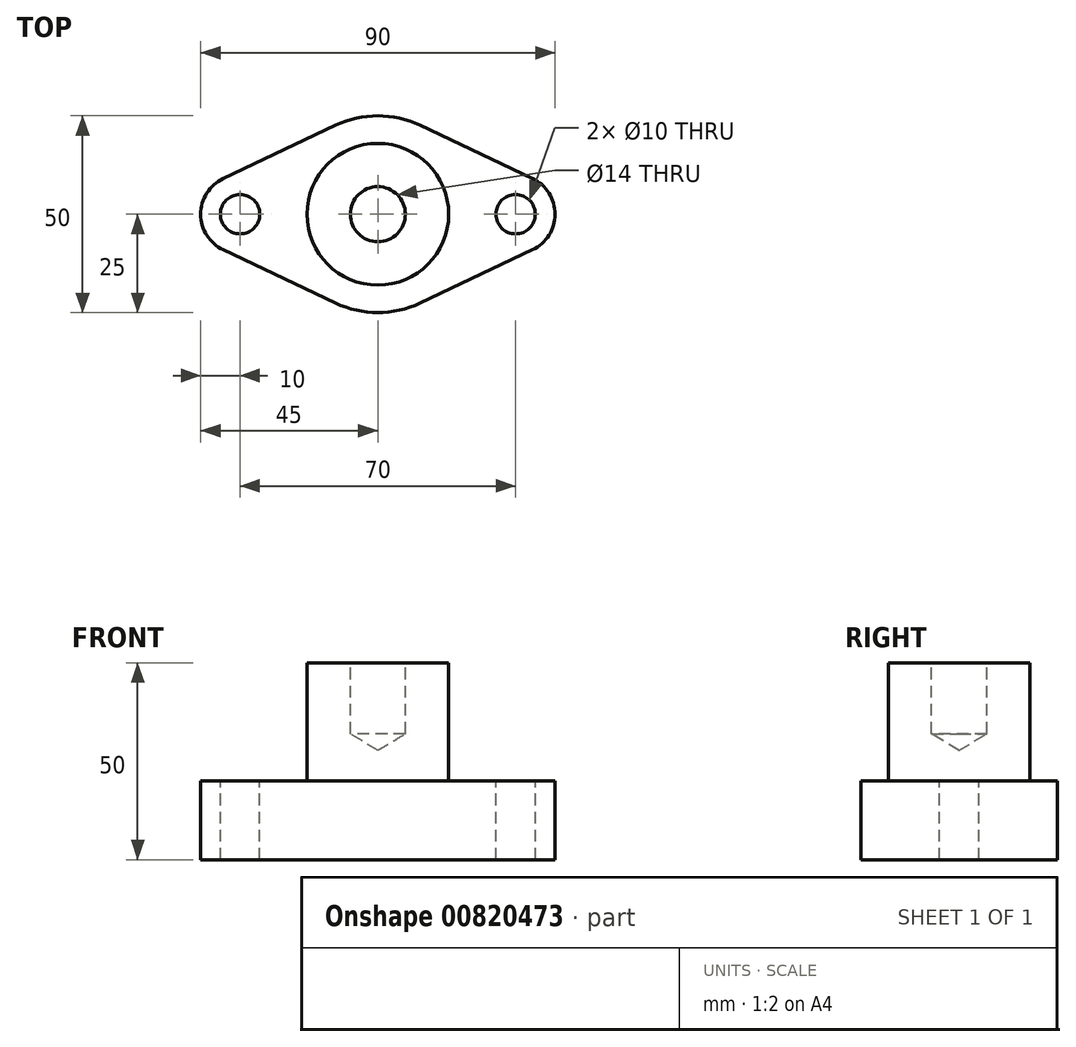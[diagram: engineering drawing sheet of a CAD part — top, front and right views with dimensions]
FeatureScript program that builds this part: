
annotation { "Feature Type Name" : "Feature", "Feature Type Description" : "" }
export const myFeature = defineFeature(function(context is Context, id is Id, definition is map)
    precondition{}
    {
        {
            var Q0;
            Q0=qCreatedBy(makeId("Top.planeOp"),FACE);
            var sketch = newSketch(context, id + "F0", { "sketchPlane" : qUnion([Q0])});
            skCircle(sketch, "E0", {"center": v(0, 0) * mm, "radius": 25 * mm});
            skPoint(sketch, "E1", {"position": v(-35, 0) * mm});
            skCircle(sketch, "E2", {"center": v(-35, 0) * mm, "radius": 10 * mm});
            skPoint(sketch, "E3", {"position": v(35, 0) * mm});
            skCircle(sketch, "E4", {"center": v(35, 0) * mm, "radius": 10 * mm});
            skLineSegment(sketch, "E5", {"start": v(-39.29, 9.04) * mm, "end": v(-10.71, 22.59) * mm});
            skLineSegment(sketch, "E6", {"start": v(10.71, 22.59) * mm, "end": v(39.29, 9.04) * mm});
            skLineSegment(sketch, "E7", {"start": v(-39.29, -9.04) * mm, "end": v(-10.71, -22.59) * mm});
            skLineSegment(sketch, "E8", {"start": v(10.71, -22.59) * mm, "end": v(39.29, -9.04) * mm});
            skSolve(sketch);
        }
        {
            var Q0;
            {var subQ0=sQuery(id+"F0.wireOp",EDGE,"E6");Q0=makeQuery(id+"F0.imprint","IMPRINT",FACE,{"disambiguationData":[TD([[makeQuery(id+"F0.imprint","IMPRINT",EDGE,{"derivedFrom":subQ0}),-1.0]])]});}
            var Q1;
            {var subQ0=sQuery(id+"F0.wireOp",EDGE,"E8");Q1=makeQuery(id+"F0.imprint","IMPRINT",FACE,{"disambiguationData":[TD([[makeQuery(id+"F0.imprint","IMPRINT",EDGE,{"derivedFrom":subQ0}),1.0]])]});}
            var Q2;
            {var subQ0=sQuery(id+"F0.wireOp",EDGE,"E5");Q2=makeQuery(id+"F0.imprint","IMPRINT",FACE,{"disambiguationData":[TD([[makeQuery(id+"F0.imprint","IMPRINT",EDGE,{"derivedFrom":subQ0}),-1.0]])]});}
            var Q3;
            {var subQ0=sQuery(id+"F0.wireOp",EDGE,"E2");var subQ1=makeQuery(id+"F0.imprint","INTERSECT",VERTEX,{"derivedFrom":[subQ0,sQuery(id+"F0.wireOp",EDGE,"E5")]});Q3=makeQuery(id+"F0.imprint","IMPRINT",FACE,{"disambiguationData":[TD([[makeQuery(id+"F0.imprint","IMPRINT",EDGE,{"disambiguationData":[TD([[subQ1,1.0]])],"derivedFrom":subQ0}),1.0]])]});}
            var Q4;
            {var subQ0=sQuery(id+"F0.wireOp",EDGE,"E4");var subQ1=makeQuery(id+"F0.imprint","INTERSECT",VERTEX,{"derivedFrom":[subQ0,sQuery(id+"F0.wireOp",EDGE,"E6")]});Q4=makeQuery(id+"F0.imprint","IMPRINT",FACE,{"disambiguationData":[TD([[makeQuery(id+"F0.imprint","IMPRINT",EDGE,{"disambiguationData":[TD([[subQ1,-1.0]])],"derivedFrom":subQ0}),1.0]])]});}
            var Q5;
            {var subQ0=sQuery(id+"F0.wireOp",EDGE,"E7");Q5=makeQuery(id+"F0.imprint","IMPRINT",FACE,{"disambiguationData":[TD([[makeQuery(id+"F0.imprint","IMPRINT",EDGE,{"derivedFrom":subQ0}),1.0]])]});}
            var Q6;
            {var subQ0=sQuery(id+"F0.wireOp",EDGE,"E0");var subQ4=makeQuery(id+"F0.imprint","INTERSECT",VERTEX,{"derivedFrom":[subQ0,sQuery(id+"F0.wireOp",EDGE,"E6")]});Q6=makeQuery(id+"F0.imprint","IMPRINT",FACE,{"disambiguationData":[TD([[makeQuery(id+"F0.imprint","IMPRINT",EDGE,{"disambiguationData":[TD([[subQ4,1.0]])],"derivedFrom":subQ0}),1.0]])]});}
            extrude(context, id + "F1", {"entities" : qUnion([Q0, Q1, Q2, Q3, Q4, Q5, Q6]), "endBound" : BoundingType.SYMMETRIC, "depth" : 20 * mm, "offsetDistance" : 25 * mm});
        }
        {
            var Q0;
            Q0=makeQuery(id+"F1.opExtrude","CAP_FACE",FACE,{"disambiguationData":[OSD([sQuery(id+"F0.wireOp",EDGE,"E0"),sQuery(id+"F0.wireOp",EDGE,"E2"),sQuery(id+"F0.wireOp",EDGE,"E4"),sQuery(id+"F0.wireOp",EDGE,"E5"),sQuery(id+"F0.wireOp",EDGE,"E6"),sQuery(id+"F0.wireOp",EDGE,"E7"),sQuery(id+"F0.wireOp",EDGE,"E8")])],"isStart":false});
            var sketch = newSketch(context, id + "F2", { "sketchPlane" : qUnion([Q0])});
            skPoint(sketch, "E9", {"position": v(-35, 0) * mm});
            skPoint(sketch, "E10", {"position": v(35, 0) * mm});
            skSolve(sketch);
        }
        {
            var Q0;
            Q0=sQuery(id+"F2.wireOp",VERTEX,"E9");
            var Q1;
            Q1=sQuery(id+"F2.wireOp",VERTEX,"E10");
            var Q2;
            Q2=makeQuery(id+"F1.opExtrude","SWEPT_BODY",BODY,{"disambiguationData":[OSD([sQuery(id+"F0.wireOp",EDGE,"E0"),sQuery(id+"F0.wireOp",EDGE,"E2"),sQuery(id+"F0.wireOp",EDGE,"E4"),sQuery(id+"F0.wireOp",EDGE,"E5"),sQuery(id+"F0.wireOp",EDGE,"E6"),sQuery(id+"F0.wireOp",EDGE,"E7"),sQuery(id+"F0.wireOp",EDGE,"E8")])]});
            hole(context, id + "F3", {"style" : HoleStyle.SIMPLE, "endStyle" : HoleEndStyle.THROUGH, "holeDiameter" : 10 * mm, "majorDiameter" : 5 * mm, "isTappedThrough" : true, "tappedDepth" : 12 * mm, "tapClearance" : 3, "startFromSketch" : true, "locations" : qUnion([Q0, Q1]), "scope" : qUnion([Q2])});
        }
        {
            var Q0;
            Q0=makeQuery(id+"F1.opExtrude","CAP_FACE",FACE,{"disambiguationData":[OSD([sQuery(id+"F0.wireOp",EDGE,"E0"),sQuery(id+"F0.wireOp",EDGE,"E2"),sQuery(id+"F0.wireOp",EDGE,"E4"),sQuery(id+"F0.wireOp",EDGE,"E5"),sQuery(id+"F0.wireOp",EDGE,"E6"),sQuery(id+"F0.wireOp",EDGE,"E7"),sQuery(id+"F0.wireOp",EDGE,"E8")])],"isStart":false});
            var sketch = newSketch(context, id + "F4", { "sketchPlane" : qUnion([Q0])});
            skCircle(sketch, "E11", {"center": v(0, 0) * mm, "radius": 18 * mm});
            skSolve(sketch);
        }
        {
            var Q0;
            Q0=makeQuery(id+"F4.imprint","IMPRINT",FACE,{"disambiguationData":[TD([[makeQuery(id+"F4.imprint","IMPRINT",EDGE,{"derivedFrom":sQuery(id+"F4.wireOp",EDGE,"E11")}),1.0]])]});
            extrude(context, id + "F5", {"entities" : qUnion([Q0]), "operationType" : NewBodyOperationType.ADD, "depth" : 30 * mm, "offsetDistance" : 25 * mm});
        }
        {
            var Q0;
            Q0=makeQuery(id+"F5.opExtrude","CAP_FACE",FACE,{"disambiguationData":[OSD([sQuery(id+"F4.wireOp",EDGE,"E11")])],"isStart":false});
            var sketch = newSketch(context, id + "F6", { "sketchPlane" : qUnion([Q0])});
            skPoint(sketch, "E12", {"position": v(0, 0) * mm});
            skSolve(sketch);
        }
        {
            var Q0;
            Q0=sQuery(id+"F6.wireOp",VERTEX,"E12");
            var Q1;
            Q1=makeQuery(id+"F1.opExtrude","SWEPT_BODY",BODY,{"disambiguationData":[OSD([sQuery(id+"F0.wireOp",EDGE,"E0"),sQuery(id+"F0.wireOp",EDGE,"E2"),sQuery(id+"F0.wireOp",EDGE,"E4"),sQuery(id+"F0.wireOp",EDGE,"E5"),sQuery(id+"F0.wireOp",EDGE,"E6"),sQuery(id+"F0.wireOp",EDGE,"E7"),sQuery(id+"F0.wireOp",EDGE,"E8")])]});
            hole(context, id + "F7", {"style" : HoleStyle.SIMPLE, "endStyle" : HoleEndStyle.BLIND, "standardTappedOrClearance" : lookupTablePath({ "standard" : "ISO", "engagement" : "75%", "pitch" : "2 mm", "size" : "M16", "type" : "Tapped" }), "standardBlindInLast" : lookupTablePath({ "standard" : "ISO", "engagement" : "75%", "pitch" : "2 mm", "size" : "M16", "type" : "Tapped" }), "holeDiameter" : 14 * mm, "majorDiameter" : 16 * mm, "showTappedDepth" : true, "holeDepth" : 18 * mm, "isTappedThrough" : true, "tappedDepth" : 12 * mm, "tapClearance" : 3, "startFromSketch" : true, "locations" : qUnion([Q0]), "scope" : qUnion([Q1])});
        }
    });
